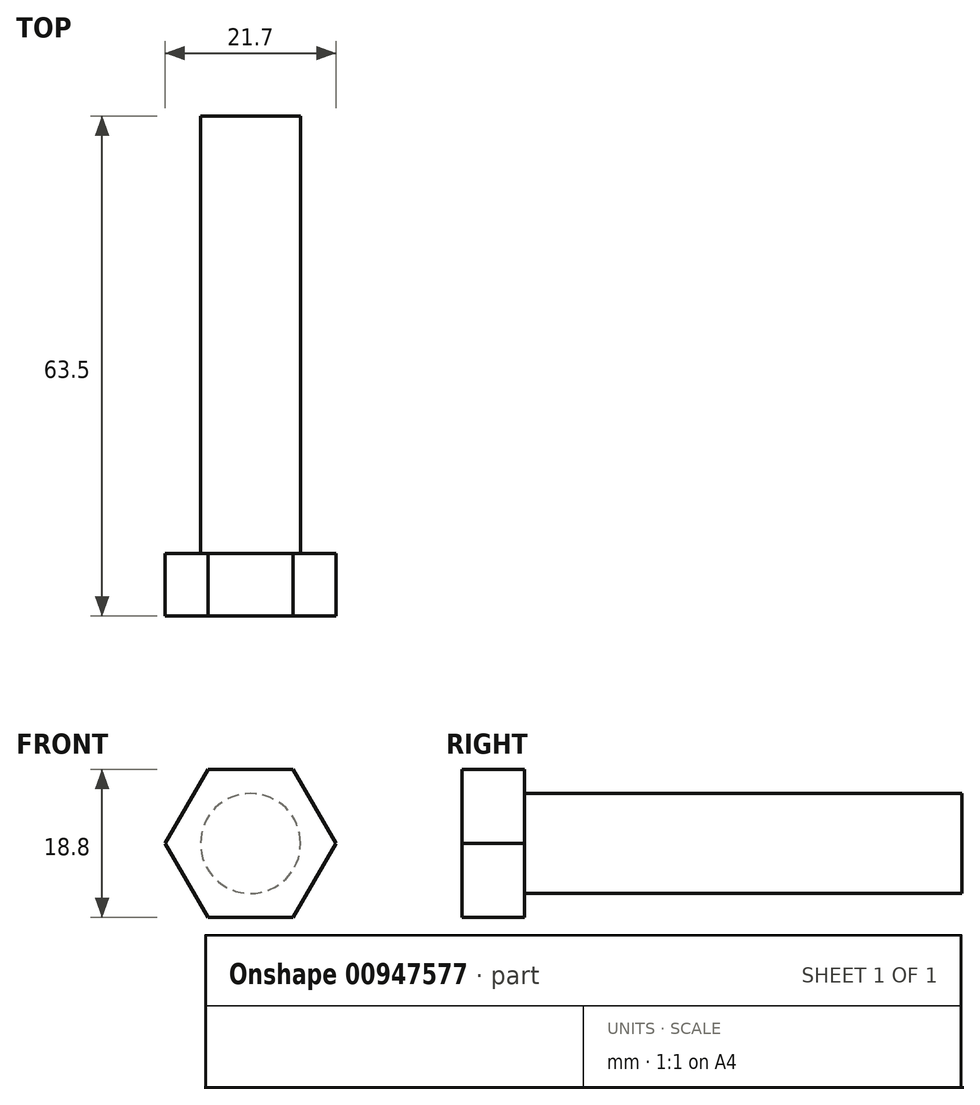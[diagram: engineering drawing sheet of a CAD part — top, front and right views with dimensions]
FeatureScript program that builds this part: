
annotation { "Feature Type Name" : "Feature", "Feature Type Description" : "" }
export const myFeature = defineFeature(function(context is Context, id is Id, definition is map)
    precondition{}
    {
        {
            var Q0;
            Q0=qCreatedBy(makeId("Front.planeOp"),FACE);
            var sketch = newSketch(context, id + "F0", { "sketchPlane" : qUnion([Q0])});
            skCircle(sketch, "E0", {"center": v(0, 0) * mm, "radius": 6.35 * mm});
            skSolve(sketch);
        }
        {
            var Q0;
            Q0 = qSketchRegion(id + "F0", true);
            extrude(context, id + "F1", {"entities" : qUnion([Q0]), "oppositeDirection" : true, "depth" : 55.56 * mm, "offsetDistance" : 25.4 * mm});
        }
        {
            var Q0;
            Q0=makeQuery(id+"F1.opExtrude","CAP_FACE",FACE,{"disambiguationData":[OSD([sQuery(id+"F0.wireOp",EDGE,"E0")])],"isStart":true});
            var sketch = newSketch(context, id + "F2", { "sketchPlane" : qUnion([Q0])});
            skCircle(sketch, "E1.cCircle", {"center": v(0, 0) * mm, "radius": 9.4 * mm, "construction": true});
            skLineSegment(sketch, "E1.0", {"start": v(-5.43, 9.4) * mm, "end": v(5.43, 9.4) * mm});
            skLineSegment(sketch, "E1.1", {"start": v(5.43, 9.4) * mm, "end": v(10.85, 0) * mm});
            skLineSegment(sketch, "E1.2", {"start": v(10.85, 0) * mm, "end": v(5.43, -9.4) * mm});
            skLineSegment(sketch, "E1.3", {"start": v(5.43, -9.4) * mm, "end": v(-5.43, -9.4) * mm});
            skLineSegment(sketch, "E1.4", {"start": v(-5.43, -9.4) * mm, "end": v(-10.85, 0) * mm});
            skLineSegment(sketch, "E1.5", {"start": v(-10.85, 0) * mm, "end": v(-5.43, 9.4) * mm});
            skPoint(sketch, "E1.0.midPoint", {"position": v(0, 9.4) * mm});
            skSolve(sketch);
        }
        {
            var Q0;
            Q0 = qSketchRegion(id + "F2", true);
            extrude(context, id + "F3", {"entities" : qUnion([Q0]), "operationType" : NewBodyOperationType.ADD, "depth" : 7.94 * mm, "offsetDistance" : 25.4 * mm});
        }
    });
